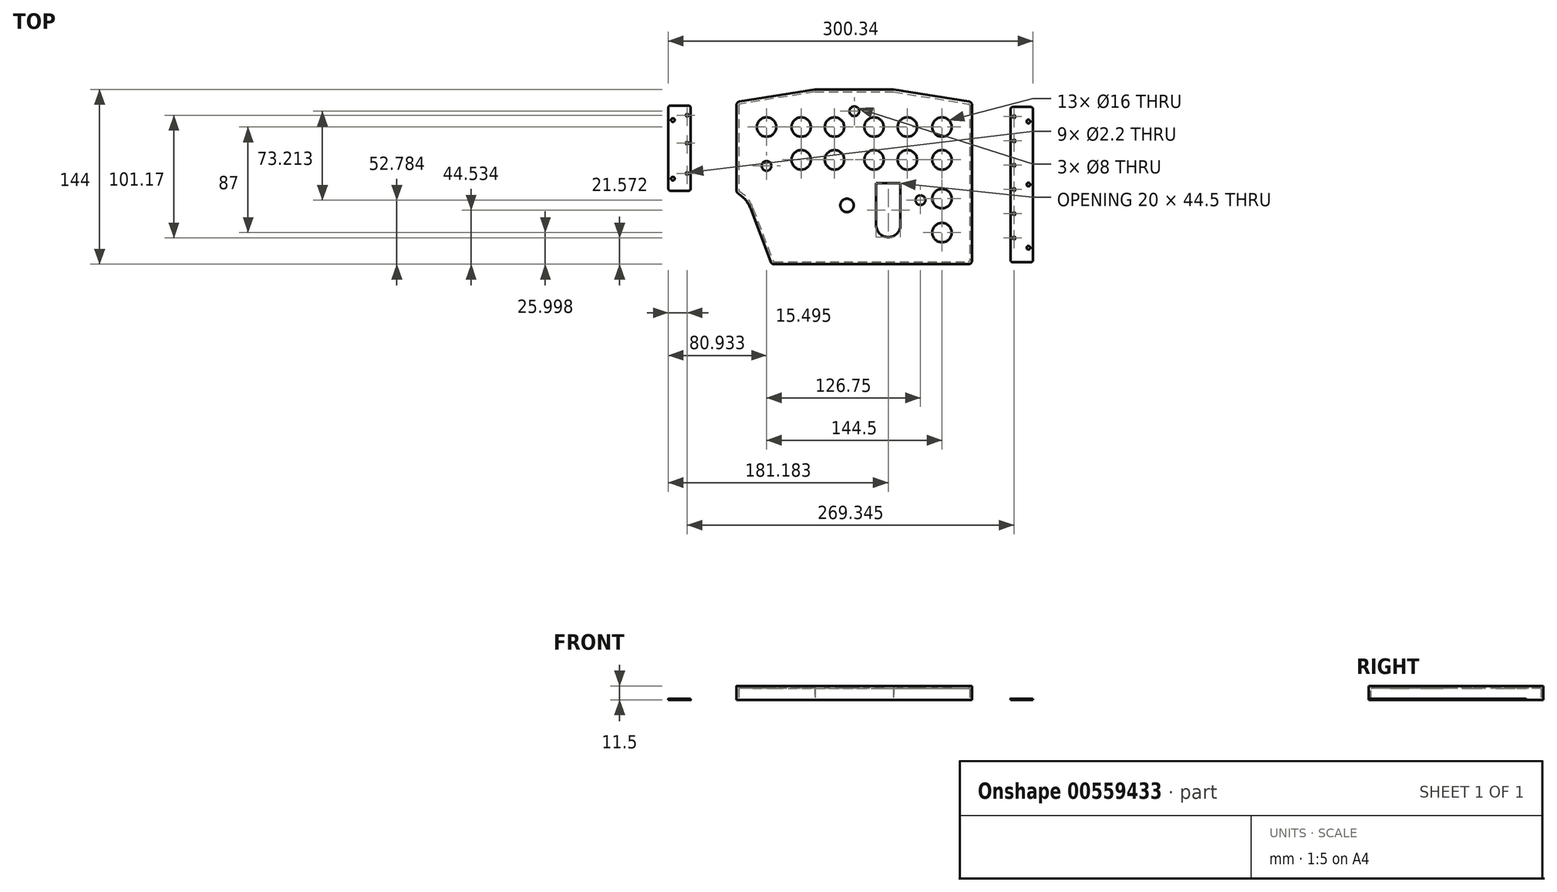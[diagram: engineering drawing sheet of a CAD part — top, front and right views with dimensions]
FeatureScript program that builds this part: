
annotation { "Feature Type Name" : "Feature", "Feature Type Description" : "" }
export const myFeature = defineFeature(function(context is Context, id is Id, definition is map)
    precondition{}
    {
        {
            var Q0;
            Q0=qCreatedBy(makeId("Top.planeOp"),FACE);
            var sketch = newSketch(context, id + "F0", { "sketchPlane" : qUnion([Q0])});
            skLineSegment(sketch, "E0.top", {"start": v(174.33, -109.34) * mm, "end": v(334.33, -109.34) * mm});
            skLineSegment(sketch, "E0.left", {"start": v(143.33, 21.7) * mm, "end": v(143.33, -48.57) * mm});
            skLineSegment(sketch, "E0.right", {"start": v(337.33, 21.7) * mm, "end": v(337.33, -106.34) * mm});
            skLineSegment(sketch, "E1", {"start": v(154.92, -63.5) * mm, "end": v(171.53, -107.4) * mm});
            skLineSegment(sketch, "E2", {"start": v(207.83, 34.66) * mm, "end": v(272.83, 34.66) * mm});
            skLineSegment(sketch, "E3", {"start": v(272.83, 34.66) * mm, "end": v(334.81, 24.66) * mm});
            skLineSegment(sketch, "E4", {"start": v(207.83, 34.66) * mm, "end": v(145.85, 24.66) * mm});
            skPoint(sketch, "E5.visualSharp", {"position": v(143.33, 24.25) * mm});
            skArc(sketch, "E5.filletArc", {"start": v(145.85, 24.66) * mm, "mid": v(144.05, 23.64) * mm, "end": v(143.33, 21.7) * mm});
            skPoint(sketch, "E6.visualSharp", {"position": v(337.33, 24.25) * mm});
            skArc(sketch, "E6.filletArc", {"start": v(337.33, 21.7) * mm, "mid": v(336.62, 23.64) * mm, "end": v(334.81, 24.66) * mm});
            skPoint(sketch, "E7.visualSharp", {"position": v(337.33, -109.34) * mm});
            skArc(sketch, "E7.filletArc", {"start": v(334.33, -109.34) * mm, "mid": v(336.45, -108.46) * mm, "end": v(337.33, -106.34) * mm});
            skPoint(sketch, "E8.visualSharp", {"position": v(172.26, -109.34) * mm});
            skArc(sketch, "E8.filletArc", {"start": v(171.53, -107.4) * mm, "mid": v(172.63, -108.8) * mm, "end": v(174.33, -109.34) * mm});
            skArc(sketch, "E9", {"start": v(154.92, -63.5) * mm, "mid": v(150.85, -56.47) * mm, "end": v(144.75, -51.12) * mm});
            skPoint(sketch, "E10.visualSharp", {"position": v(143.33, -50.3) * mm});
            skArc(sketch, "E10.filletArc", {"start": v(143.33, -48.57) * mm, "mid": v(143.7, -50.03) * mm, "end": v(144.75, -51.12) * mm});
            skSolve(sketch);
        }
        {
            var Q0;
            Q0=qSketchRegion(id+"F0",true);
            extrude(context, id + "F1", {"entities" : qUnion([Q0]), "depth" : 11.5 * mm});
        }
        {
            var Q0;
            Q0=makeQuery(id+"F1.opExtrude","CAP_FACE",FACE,{"disambiguationData":[OSD([sQuery(id+"F0.wireOp",EDGE,"E0.top"),sQuery(id+"F0.wireOp",EDGE,"E0.left"),sQuery(id+"F0.wireOp",EDGE,"E0.right"),sQuery(id+"F0.wireOp",EDGE,"E1"),sQuery(id+"F0.wireOp",EDGE,"E2"),sQuery(id+"F0.wireOp",EDGE,"E3"),sQuery(id+"F0.wireOp",EDGE,"E4"),sQuery(id+"F0.wireOp",EDGE,"E5.filletArc"),sQuery(id+"F0.wireOp",EDGE,"E6.filletArc"),sQuery(id+"F0.wireOp",EDGE,"E7.filletArc"),sQuery(id+"F0.wireOp",EDGE,"E8.filletArc"),sQuery(id+"F0.wireOp",EDGE,"E9"),sQuery(id+"F0.wireOp",EDGE,"E10.filletArc")])],"isStart":true});
            shell(context, id + "F2", {"entities" : qUnion([Q0]), "thickness" : 2 * mm});
        }
        {
            var Q0;
            Q0=makeQuery(id+"F1.opExtrude","CAP_FACE",FACE,{"disambiguationData":[OSD([sQuery(id+"F0.wireOp",EDGE,"E0.top"),sQuery(id+"F0.wireOp",EDGE,"E0.left"),sQuery(id+"F0.wireOp",EDGE,"E0.right"),sQuery(id+"F0.wireOp",EDGE,"E1"),sQuery(id+"F0.wireOp",EDGE,"E2"),sQuery(id+"F0.wireOp",EDGE,"E3"),sQuery(id+"F0.wireOp",EDGE,"E4"),sQuery(id+"F0.wireOp",EDGE,"E5.filletArc"),sQuery(id+"F0.wireOp",EDGE,"E6.filletArc"),sQuery(id+"F0.wireOp",EDGE,"E7.filletArc"),sQuery(id+"F0.wireOp",EDGE,"E8.filletArc"),sQuery(id+"F0.wireOp",EDGE,"E9"),sQuery(id+"F0.wireOp",EDGE,"E10.filletArc")])],"isStart":false});
            var sketch = newSketch(context, id + "F3", { "sketchPlane" : qUnion([Q0])});
            skLineSegment(sketch, "E11.bottom", {"start": v(150.33, 21.66) * mm, "end": v(331.33, 21.66) * mm});
            skLineSegment(sketch, "E11.top", {"start": v(185.56, -101.56) * mm, "end": v(331.33, -101.56) * mm});
            skLineSegment(sketch, "E11.left", {"start": v(150.33, 21.66) * mm, "end": v(150.33, -46.56) * mm});
            skLineSegment(sketch, "E11.right", {"start": v(331.33, 21.66) * mm, "end": v(331.33, -101.56) * mm});
            skLineSegment(sketch, "E12", {"start": v(150.33, -46.56) * mm, "end": v(185.56, -46.56) * mm});
            skLineSegment(sketch, "E13", {"start": v(185.56, -46.56) * mm, "end": v(185.56, -101.56) * mm});
            skCircle(sketch, "E14", {"center": v(168.08, 3.66) * mm, "radius": 8 * mm});
            skCircle(sketch, "E15", {"center": v(196.58, 3.66) * mm, "radius": 8 * mm});
            skCircle(sketch, "E16", {"center": v(224.08, 3.66) * mm, "radius": 8 * mm});
            skCircle(sketch, "E17", {"center": v(234.33, -60.84) * mm, "radius": 5.5 * mm});
            skCircle(sketch, "E18", {"center": v(256.58, 3.66) * mm, "radius": 8 * mm});
            skCircle(sketch, "E19", {"center": v(284.08, 3.66) * mm, "radius": 8 * mm});
            skCircle(sketch, "E20", {"center": v(312.58, 3.66) * mm, "radius": 8 * mm});
            skCircle(sketch, "E21", {"center": v(312.58, -55.34) * mm, "radius": 8 * mm});
            skCircle(sketch, "E22", {"center": v(312.58, -83.34) * mm, "radius": 8 * mm});
            skLineSegment(sketch, "E23.top", {"start": v(210.83, 28.66) * mm, "end": v(270.83, 28.66) * mm});
            skLineSegment(sketch, "E23.left", {"start": v(210.83, 21.66) * mm, "end": v(210.83, 28.66) * mm});
            skLineSegment(sketch, "E23.right", {"start": v(270.83, 21.66) * mm, "end": v(270.83, 28.66) * mm});
            skLineSegment(sketch, "E24.left", {"start": v(258.33, -42.56) * mm, "end": v(258.33, -77.06) * mm});
            skLineSegment(sketch, "E24.right", {"start": v(278.33, -42.56) * mm, "end": v(278.33, -77.06) * mm});
            skLineSegment(sketch, "E25", {"start": v(258.33, -42.56) * mm, "end": v(278.33, -42.56) * mm});
            skCircle(sketch, "E26", {"center": v(240.33, 16.66) * mm, "radius": 4 * mm});
            skCircle(sketch, "E27", {"center": v(294.83, -56.56) * mm, "radius": 4 * mm});
            skLineSegment(sketch, "E28.bottom", {"start": v(150.33, 21.66) * mm, "end": v(149.33, 21.66) * mm});
            skLineSegment(sketch, "E28.top", {"start": v(150.33, -46.56) * mm, "end": v(147.33, -46.56) * mm});
            skLineSegment(sketch, "E28.right", {"start": v(147.33, 19.66) * mm, "end": v(147.33, -46.56) * mm});
            skLineSegment(sketch, "E29.bottom", {"start": v(147.33, -46.56) * mm, "end": v(185.56, -46.56) * mm});
            skLineSegment(sketch, "E29.top", {"start": v(149.33, -49.56) * mm, "end": v(185.56, -49.56) * mm});
            skLineSegment(sketch, "E29.left", {"start": v(147.33, -46.56) * mm, "end": v(147.33, -47.56) * mm});
            skLineSegment(sketch, "E29.right", {"start": v(185.56, -46.56) * mm, "end": v(185.56, -49.56) * mm});
            skLineSegment(sketch, "E30.bottom", {"start": v(185.56, -101.56) * mm, "end": v(182.56, -101.56) * mm});
            skLineSegment(sketch, "E30.top", {"start": v(185.56, -49.56) * mm, "end": v(182.56, -49.56) * mm});
            skLineSegment(sketch, "E30.left", {"start": v(185.56, -101.56) * mm, "end": v(185.56, -49.56) * mm});
            skLineSegment(sketch, "E30.right", {"start": v(182.56, -101.56) * mm, "end": v(182.56, -49.56) * mm});
            skLineSegment(sketch, "E31.bottom", {"start": v(182.56, -101.56) * mm, "end": v(254.56, -101.56) * mm});
            skLineSegment(sketch, "E31.top", {"start": v(182.56, -104.56) * mm, "end": v(254.56, -104.56) * mm});
            skLineSegment(sketch, "E31.left", {"start": v(182.56, -101.56) * mm, "end": v(182.56, -104.56) * mm});
            skLineSegment(sketch, "E31.right", {"start": v(254.56, -101.56) * mm, "end": v(254.56, -104.56) * mm});
            skLineSegment(sketch, "E32.bottom", {"start": v(270.33, -101.56) * mm, "end": v(306.33, -101.56) * mm});
            skLineSegment(sketch, "E32.top", {"start": v(270.33, -104.56) * mm, "end": v(306.33, -104.56) * mm});
            skLineSegment(sketch, "E32.left", {"start": v(270.33, -101.56) * mm, "end": v(270.33, -104.56) * mm});
            skLineSegment(sketch, "E32.right", {"start": v(306.33, -101.56) * mm, "end": v(306.33, -104.56) * mm});
            skLineSegment(sketch, "E33.bottom", {"start": v(331.33, 21.66) * mm, "end": v(332.33, 21.66) * mm});
            skLineSegment(sketch, "E33.top", {"start": v(331.33, -101.56) * mm, "end": v(334.33, -101.56) * mm});
            skLineSegment(sketch, "E33.right", {"start": v(334.33, 19.66) * mm, "end": v(334.33, -101.56) * mm});
            skLineSegment(sketch, "E34.bottom", {"start": v(321.33, -101.56) * mm, "end": v(334.33, -101.56) * mm});
            skLineSegment(sketch, "E34.top", {"start": v(321.33, -104.56) * mm, "end": v(334.33, -104.56) * mm});
            skLineSegment(sketch, "E34.left", {"start": v(321.33, -101.56) * mm, "end": v(321.33, -104.56) * mm});
            skLineSegment(sketch, "E34.right", {"start": v(334.33, -101.56) * mm, "end": v(334.33, -104.56) * mm});
            skLineSegment(sketch, "E35.bottom", {"start": v(210.83, 28.66) * mm, "end": v(209.83, 28.66) * mm});
            skLineSegment(sketch, "E35.top", {"start": v(210.83, 21.66) * mm, "end": v(209.83, 21.66) * mm});
            skLineSegment(sketch, "E35.left", {"start": v(210.83, 28.66) * mm, "end": v(210.83, 21.66) * mm});
            skLineSegment(sketch, "E35.right", {"start": v(209.83, 28.66) * mm, "end": v(209.83, 21.66) * mm});
            skLineSegment(sketch, "E36.bottom", {"start": v(209.83, 21.66) * mm, "end": v(203.83, 21.66) * mm});
            skLineSegment(sketch, "E36.top", {"start": v(209.83, 22.66) * mm, "end": v(203.83, 22.66) * mm});
            skLineSegment(sketch, "E36.left", {"start": v(209.83, 21.66) * mm, "end": v(209.83, 22.66) * mm});
            skLineSegment(sketch, "E36.right", {"start": v(203.83, 21.66) * mm, "end": v(203.83, 22.66) * mm});
            skLineSegment(sketch, "E37.bottom", {"start": v(270.83, 28.66) * mm, "end": v(271.83, 28.66) * mm});
            skLineSegment(sketch, "E37.top", {"start": v(270.83, 21.66) * mm, "end": v(271.83, 21.66) * mm});
            skLineSegment(sketch, "E37.left", {"start": v(270.83, 28.66) * mm, "end": v(270.83, 21.66) * mm});
            skLineSegment(sketch, "E37.right", {"start": v(271.83, 28.66) * mm, "end": v(271.83, 21.66) * mm});
            skLineSegment(sketch, "E38.bottom", {"start": v(271.83, 21.66) * mm, "end": v(277.83, 21.66) * mm});
            skLineSegment(sketch, "E38.top", {"start": v(271.83, 22.66) * mm, "end": v(277.83, 22.66) * mm});
            skLineSegment(sketch, "E38.left", {"start": v(271.83, 21.66) * mm, "end": v(271.83, 22.66) * mm});
            skLineSegment(sketch, "E38.right", {"start": v(277.83, 21.66) * mm, "end": v(277.83, 22.66) * mm});
            skPoint(sketch, "E39.visualSharp", {"position": v(147.33, 21.66) * mm});
            skArc(sketch, "E39.filletArc", {"start": v(149.33, 21.66) * mm, "mid": v(147.92, 21.07) * mm, "end": v(147.33, 19.66) * mm});
            skPoint(sketch, "E40.visualSharp", {"position": v(334.33, 21.66) * mm});
            skArc(sketch, "E40.filletArc", {"start": v(334.33, 19.66) * mm, "mid": v(333.75, 21.07) * mm, "end": v(332.33, 21.66) * mm});
            skPoint(sketch, "E41.visualSharp", {"position": v(147.33, -49.56) * mm});
            skArc(sketch, "E41.filletArc", {"start": v(147.33, -47.56) * mm, "mid": v(147.92, -48.97) * mm, "end": v(149.33, -49.56) * mm});
            skCircle(sketch, "E42", {"center": v(153.08, 13.66) * mm, "radius": 1.5 * mm, "construction": true});
            skCircle(sketch, "E43", {"center": v(153.08, -9.34) * mm, "radius": 1.5 * mm, "construction": true});
            skLineSegment(sketch, "E44.bottom", {"start": v(155.33, 16.16) * mm, "end": v(160.33, 16.16) * mm, "construction": true});
            skLineSegment(sketch, "E44.top", {"start": v(155.33, -8.84) * mm, "end": v(160.33, -8.84) * mm, "construction": true});
            skLineSegment(sketch, "E44.left", {"start": v(155.33, 16.16) * mm, "end": v(155.33, -8.84) * mm, "construction": true});
            skLineSegment(sketch, "E44.right", {"start": v(160.33, 16.16) * mm, "end": v(160.33, -8.84) * mm, "construction": true});
            skCircle(sketch, "E45", {"center": v(157.83, 11.16) * mm, "radius": 1 * mm, "construction": true});
            skPoint(sketch, "E45.centerSnap0", {"position": v(157.83, 16.16) * mm});
            skCircle(sketch, "E46", {"center": v(157.83, -3.84) * mm, "radius": 1 * mm, "construction": true});
            skCircle(sketch, "E47", {"center": v(153.08, -34.34) * mm, "radius": 1.5 * mm, "construction": true});
            skLineSegment(sketch, "E48.bottom", {"start": v(320.83, 16.16) * mm, "end": v(325.83, 16.16) * mm, "construction": true});
            skLineSegment(sketch, "E48.top", {"start": v(320.83, -8.84) * mm, "end": v(325.83, -8.84) * mm, "construction": true});
            skLineSegment(sketch, "E48.left", {"start": v(320.83, 16.16) * mm, "end": v(320.83, -8.84) * mm, "construction": true});
            skLineSegment(sketch, "E48.right", {"start": v(325.83, 16.16) * mm, "end": v(325.83, -8.84) * mm, "construction": true});
            skCircle(sketch, "E49", {"center": v(323.33, 11.16) * mm, "radius": 1 * mm});
            skPoint(sketch, "E49.centerSnap0", {"position": v(323.33, 16.16) * mm});
            skCircle(sketch, "E50", {"center": v(323.33, -3.84) * mm, "radius": 1 * mm});
            skLineSegment(sketch, "E51", {"start": v(157.98, 3.66) * mm, "end": v(328.03, 3.66) * mm, "construction": true});
            skCircle(sketch, "E52", {"center": v(234.33, -60.84) * mm, "radius": 12.5 * mm, "construction": true});
            skLineSegment(sketch, "E53", {"start": v(268.33, -87.06) * mm, "end": v(268.33, -87.06) * mm});
            skCircle(sketch, "E54", {"center": v(196.58, -23.34) * mm, "radius": 8 * mm});
            skCircle(sketch, "E55", {"center": v(168.08, -28.34) * mm, "radius": 4 * mm});
            skCircle(sketch, "E56", {"center": v(224.08, -23.34) * mm, "radius": 8 * mm});
            skCircle(sketch, "E57", {"center": v(256.58, -23.34) * mm, "radius": 8 * mm});
            skCircle(sketch, "E58", {"center": v(284.08, -23.34) * mm, "radius": 8 * mm});
            skCircle(sketch, "E59", {"center": v(312.58, -23.34) * mm, "radius": 8 * mm});
            skCircle(sketch, "E60", {"center": v(268.33, -71.06) * mm, "radius": 8 * mm, "construction": true});
            skPoint(sketch, "E60.centerSnap0", {"position": v(268.33, -42.56) * mm});
            skPoint(sketch, "E61.visualSharp", {"position": v(258.33, -87.06) * mm});
            skArc(sketch, "E61.filletArc", {"start": v(258.33, -77.06) * mm, "mid": v(261.26, -84.13) * mm, "end": v(268.33, -87.06) * mm});
            skPoint(sketch, "E62.visualSharp", {"position": v(278.33, -87.06) * mm});
            skArc(sketch, "E62.filletArc", {"start": v(268.33, -87.06) * mm, "mid": v(275.4, -84.13) * mm, "end": v(278.33, -77.06) * mm});
            skSolve(sketch);
        }
        {
            var Q0;
            Q0=makeQuery(id+"F3.imprint","IMPRINT",FACE,{"disambiguationData":[TD([[makeQuery(id+"F3.imprint","IMPRINT",EDGE,{"derivedFrom":sQuery(id+"F3.wireOp",EDGE,"E14")}),1.0]])]});
            var Q1;
            Q1=makeQuery(id+"F3.imprint","IMPRINT",FACE,{"disambiguationData":[TD([[makeQuery(id+"F3.imprint","IMPRINT",EDGE,{"derivedFrom":sQuery(id+"F3.wireOp",EDGE,"E15")}),1.0]])]});
            var Q2;
            Q2=makeQuery(id+"F3.imprint","IMPRINT",FACE,{"disambiguationData":[TD([[makeQuery(id+"F3.imprint","IMPRINT",EDGE,{"derivedFrom":sQuery(id+"F3.wireOp",EDGE,"E16")}),1.0]])]});
            var Q3;
            Q3=makeQuery(id+"F3.imprint","IMPRINT",FACE,{"disambiguationData":[TD([[makeQuery(id+"F3.imprint","IMPRINT",EDGE,{"derivedFrom":sQuery(id+"F3.wireOp",EDGE,"E18")}),1.0]])]});
            var Q4;
            Q4=makeQuery(id+"F3.imprint","IMPRINT",FACE,{"disambiguationData":[TD([[makeQuery(id+"F3.imprint","IMPRINT",EDGE,{"derivedFrom":sQuery(id+"F3.wireOp",EDGE,"E19")}),1.0]])]});
            var Q5;
            Q5=makeQuery(id+"F3.imprint","IMPRINT",FACE,{"disambiguationData":[TD([[makeQuery(id+"F3.imprint","IMPRINT",EDGE,{"derivedFrom":sQuery(id+"F3.wireOp",EDGE,"E20")}),1.0]])]});
            var Q6;
            Q6=makeQuery(id+"F3.imprint","IMPRINT",FACE,{"disambiguationData":[TD([[makeQuery(id+"F3.imprint","IMPRINT",EDGE,{"derivedFrom":sQuery(id+"F3.wireOp",EDGE,"182ebfe6-2736-47e7-aa4b-23692cbbae48")}),1.0]])]});
            var Q7;
            Q7=makeQuery(id+"F3.imprint","IMPRINT",FACE,{"disambiguationData":[TD([[makeQuery(id+"F3.imprint","IMPRINT",EDGE,{"derivedFrom":sQuery(id+"F3.wireOp",EDGE,"e7df0eac-41cd-404f-bdd1-8c65fee716b7")}),1.0]])]});
            var Q8;
            Q8=makeQuery(id+"F3.imprint","IMPRINT",FACE,{"disambiguationData":[TD([[makeQuery(id+"F3.imprint","IMPRINT",EDGE,{"derivedFrom":sQuery(id+"F3.wireOp",EDGE,"6b2fa6bf-2d88-4192-aa23-f9972aa437f7")}),1.0]])]});
            var Q9;
            Q9=makeQuery(id+"F3.imprint","IMPRINT",FACE,{"disambiguationData":[TD([[makeQuery(id+"F3.imprint","IMPRINT",EDGE,{"derivedFrom":sQuery(id+"F3.wireOp",EDGE,"76bc2124-5548-41a5-9276-e67c2ab8353c")}),1.0]])]});
            var Q10;
            Q10=makeQuery(id+"F3.imprint","IMPRINT",FACE,{"disambiguationData":[TD([[makeQuery(id+"F3.imprint","IMPRINT",EDGE,{"derivedFrom":sQuery(id+"F3.wireOp",EDGE,"525520f9-84c5-4c3a-afae-55c33ce15ad5")}),1.0]])]});
            var Q11;
            Q11=makeQuery(id+"F3.imprint","IMPRINT",FACE,{"disambiguationData":[TD([[makeQuery(id+"F3.imprint","IMPRINT",EDGE,{"derivedFrom":sQuery(id+"F3.wireOp",EDGE,"E24.left")}),1.0]])]});
            var Q12;
            Q12=makeQuery(id+"F3.imprint","IMPRINT",FACE,{"disambiguationData":[TD([[makeQuery(id+"F3.imprint","IMPRINT",EDGE,{"derivedFrom":sQuery(id+"F3.wireOp",EDGE,"E21")}),1.0]])]});
            var Q13;
            Q13=makeQuery(id+"F3.imprint","IMPRINT",FACE,{"disambiguationData":[TD([[makeQuery(id+"F3.imprint","IMPRINT",EDGE,{"derivedFrom":sQuery(id+"F3.wireOp",EDGE,"E22")}),1.0]])]});
            var Q14;
            Q14=makeQuery(id+"F3.imprint","IMPRINT",FACE,{"disambiguationData":[TD([[makeQuery(id+"F3.imprint","IMPRINT",EDGE,{"derivedFrom":sQuery(id+"F3.wireOp",EDGE,"E17")}),1.0]])]});
            var Q15;
            Q15=makeQuery(id+"F3.imprint","IMPRINT",FACE,{"disambiguationData":[TD([[makeQuery(id+"F3.imprint","IMPRINT",EDGE,{"derivedFrom":sQuery(id+"F3.wireOp",EDGE,"E27")}),1.0]])]});
            var Q16;
            Q16=makeQuery(id+"F3.imprint","IMPRINT",FACE,{"disambiguationData":[TD([[makeQuery(id+"F3.imprint","IMPRINT",EDGE,{"derivedFrom":sQuery(id+"F3.wireOp",EDGE,"OKDoaGtq-tjQu-zaJd-eQLP-X6xpVMhiND1Y")}),1.0]])]});
            var Q17;
            Q17=makeQuery(id+"F3.imprint","IMPRINT",FACE,{"disambiguationData":[TD([[makeQuery(id+"F3.imprint","IMPRINT",EDGE,{"derivedFrom":sQuery(id+"F3.wireOp",EDGE,"E26")}),1.0]])]});
            var Q18;
            Q18=makeQuery(id+"F3.imprint","IMPRINT",FACE,{"disambiguationData":[TD([[makeQuery(id+"F3.imprint","IMPRINT",EDGE,{"derivedFrom":sQuery(id+"F3.wireOp",EDGE,"E55")}),1.0]])]});
            var Q19;
            Q19=makeQuery(id+"F3.imprint","IMPRINT",FACE,{"disambiguationData":[TD([[makeQuery(id+"F3.imprint","IMPRINT",EDGE,{"derivedFrom":sQuery(id+"F3.wireOp",EDGE,"E54")}),1.0]])]});
            var Q20;
            Q20=makeQuery(id+"F3.imprint","IMPRINT",FACE,{"disambiguationData":[TD([[makeQuery(id+"F3.imprint","IMPRINT",EDGE,{"derivedFrom":sQuery(id+"F3.wireOp",EDGE,"E56")}),1.0]])]});
            var Q21;
            Q21=makeQuery(id+"F3.imprint","IMPRINT",FACE,{"disambiguationData":[TD([[makeQuery(id+"F3.imprint","IMPRINT",EDGE,{"derivedFrom":sQuery(id+"F3.wireOp",EDGE,"E57")}),1.0]])]});
            var Q22;
            Q22=makeQuery(id+"F3.imprint","IMPRINT",FACE,{"disambiguationData":[TD([[makeQuery(id+"F3.imprint","IMPRINT",EDGE,{"derivedFrom":sQuery(id+"F3.wireOp",EDGE,"E58")}),1.0]])]});
            var Q23;
            Q23=makeQuery(id+"F3.imprint","IMPRINT",FACE,{"disambiguationData":[TD([[makeQuery(id+"F3.imprint","IMPRINT",EDGE,{"derivedFrom":sQuery(id+"F3.wireOp",EDGE,"E59")}),1.0]])]});
            extrude(context, id + "F4", {"entities" : qUnion([Q0, Q1, Q2, Q3, Q4, Q5, Q6, Q7, Q8, Q9, Q10, Q11, Q12, Q13, Q14, Q15, Q16, Q17, Q18, Q19, Q20, Q21, Q22, Q23]), "operationType" : NewBodyOperationType.REMOVE, "oppositeDirection" : true, "depth" : 5 * mm});
        }
        {
            var Q0;
            Q0=qCreatedBy(makeId("Top.planeOp"),FACE);
            var sketch = newSketch(context, id + "F5", { "sketchPlane" : qUnion([Q0])});
            skLineSegment(sketch, "E63.bottom", {"start": v(87.15, 21.4) * mm, "end": v(104.65, 21.4) * mm});
            skLineSegment(sketch, "E63.top", {"start": v(87.15, -48.87) * mm, "end": v(104.65, -48.87) * mm});
            skLineSegment(sketch, "E63.left", {"start": v(87.15, 21.4) * mm, "end": v(87.15, -48.87) * mm});
            skLineSegment(sketch, "E63.right", {"start": v(104.65, 21.4) * mm, "end": v(104.65, -48.87) * mm});
            skCircle(sketch, "E64", {"center": v(102.15, 16.4) * mm, "radius": 1 * mm, "construction": true});
            skCircle(sketch, "E65", {"center": v(102.65, 13.4) * mm, "radius": 1.1 * mm});
            skCircle(sketch, "E66", {"center": v(102.65, -9.6) * mm, "radius": 1.1 * mm});
            skCircle(sketch, "E67", {"center": v(102.65, -34.6) * mm, "radius": 1.1 * mm});
            skCircle(sketch, "E68", {"center": v(90.9, 9.4) * mm, "radius": 1.5 * mm});
            skCircle(sketch, "E69", {"center": v(90.9, -38.87) * mm, "radius": 1.5 * mm});
            skCircle(sketch, "E70", {"center": v(90.9, 9.4) * mm, "radius": 3.25 * mm, "construction": true});
            skSolve(sketch);
        }
        {
            var Q0;
            Q0=makeQuery(id+"F5.imprint","IMPRINT",FACE,{"disambiguationData":[TD([[makeQuery(id+"F5.imprint","IMPRINT",EDGE,{"derivedFrom":sQuery(id+"F5.wireOp",EDGE,"E63.bottom")}),-1.0]])]});
            extrude(context, id + "F6", {"entities" : qUnion([Q0]), "depth" : 1 * mm});
        }
        {
            var Q0;
            Q0=qCreatedBy(makeId("Top.planeOp"),FACE);
            var sketch = newSketch(context, id + "F7", { "sketchPlane" : qUnion([Q0])});
            skLineSegment(sketch, "E71.bottom", {"start": v(370, 20.23) * mm, "end": v(387.5, 20.23) * mm});
            skLineSegment(sketch, "E71.top", {"start": v(370, -107.8) * mm, "end": v(387.5, -107.8) * mm});
            skLineSegment(sketch, "E71.left", {"start": v(370, 20.23) * mm, "end": v(370, -107.8) * mm});
            skLineSegment(sketch, "E71.right", {"start": v(387.5, 20.23) * mm, "end": v(387.5, -107.8) * mm});
            skCircle(sketch, "E72", {"center": v(372, 12.23) * mm, "radius": 1.1 * mm});
            skCircle(sketch, "E73", {"center": v(372, -7.77) * mm, "radius": 1.1 * mm});
            skCircle(sketch, "E74", {"center": v(372, -27.77) * mm, "radius": 1.1 * mm});
            skCircle(sketch, "E75", {"center": v(372, -47.77) * mm, "radius": 1.1 * mm});
            skCircle(sketch, "E76", {"center": v(372, -67.77) * mm, "radius": 1.1 * mm});
            skCircle(sketch, "E77", {"center": v(372, -87.77) * mm, "radius": 1.1 * mm});
            skCircle(sketch, "E78", {"center": v(383.74, 8.23) * mm, "radius": 1.5 * mm});
            skCircle(sketch, "E79", {"center": v(383.74, -43.77) * mm, "radius": 1.5 * mm});
            skCircle(sketch, "E80", {"center": v(383.74, -95.8) * mm, "radius": 1.5 * mm});
            skSolve(sketch);
        }
        {
            var Q0;
            Q0=makeQuery(id+"F7.imprint","IMPRINT",FACE,{"disambiguationData":[TD([[makeQuery(id+"F7.imprint","IMPRINT",EDGE,{"derivedFrom":sQuery(id+"F7.wireOp",EDGE,"E71.bottom")}),-1.0]])]});
            extrude(context, id + "F8", {"entities" : qUnion([Q0]), "depth" : 1 * mm});
        }
        {
            var Q0;
            Q0=makeQuery(id+"F8.opExtrude","SWEPT_FACE",FACE,{"disambiguationData":[OSD([sQuery(id+"F7.wireOp",EDGE,"E71.left")])]});
            extrude(context, id + "F9", {"entities" : qUnion([Q0]), "operationType" : NewBodyOperationType.ADD, "depth" : 1 * mm});
        }
        {
            var Q0;
            Q0=makeQuery(id+"F6.opExtrude","SWEPT_FACE",FACE,{"disambiguationData":[OSD([sQuery(id+"F5.wireOp",EDGE,"E63.right")])]});
            extrude(context, id + "F10", {"entities" : qUnion([Q0]), "operationType" : NewBodyOperationType.ADD, "depth" : 1 * mm});
        }
        {
            var Q0;
            Q0=makeQuery(id+"F8.opExtrude","SWEPT_EDGE",EDGE,{"disambiguationData":[OSD([sQuery(id+"F7.wireOp",EDGE,"E71.bottom"),sQuery(id+"F7.wireOp",EDGE,"E71.right")])]});
            var Q1;
            Q1=makeQuery(id+"F9.opExtrude","CAP_EDGE",EDGE,{"disambiguationData":[OSD([sQuery(id+"F7.wireOp",EDGE,"E71.bottom"),sQuery(id+"F7.wireOp",EDGE,"E71.left")])],"isStart":false});
            var Q2;
            Q2=makeQuery(id+"F8.opExtrude","SWEPT_EDGE",EDGE,{"disambiguationData":[OSD([sQuery(id+"F7.wireOp",EDGE,"E71.top"),sQuery(id+"F7.wireOp",EDGE,"E71.right")])]});
            var Q3;
            Q3=makeQuery(id+"F9.opExtrude","CAP_EDGE",EDGE,{"disambiguationData":[OSD([sQuery(id+"F7.wireOp",EDGE,"E71.top"),sQuery(id+"F7.wireOp",EDGE,"E71.left")])],"isStart":false});
            var Q4;
            Q4=makeQuery(id+"F10.opExtrude","CAP_EDGE",EDGE,{"disambiguationData":[OSD([sQuery(id+"F5.wireOp",EDGE,"E63.top"),sQuery(id+"F5.wireOp",EDGE,"E63.right")])],"isStart":false});
            var Q5;
            Q5=makeQuery(id+"F6.opExtrude","SWEPT_EDGE",EDGE,{"disambiguationData":[OSD([sQuery(id+"F5.wireOp",EDGE,"E63.top"),sQuery(id+"F5.wireOp",EDGE,"E63.left")])]});
            var Q6;
            Q6=makeQuery(id+"F10.opExtrude","CAP_EDGE",EDGE,{"disambiguationData":[OSD([sQuery(id+"F5.wireOp",EDGE,"E63.bottom"),sQuery(id+"F5.wireOp",EDGE,"E63.right")])],"isStart":false});
            var Q7;
            Q7=makeQuery(id+"F6.opExtrude","SWEPT_EDGE",EDGE,{"disambiguationData":[OSD([sQuery(id+"F5.wireOp",EDGE,"E63.bottom"),sQuery(id+"F5.wireOp",EDGE,"E63.left")])]});
            fillet(context, id + "F11", {"entities" : qUnion([Q0, Q1, Q2, Q3, Q4, Q5, Q6, Q7]), "radius" : 2 * mm, "tangentPropagation" : true, "allowEdgeOverflow" : false});
        }
    });
